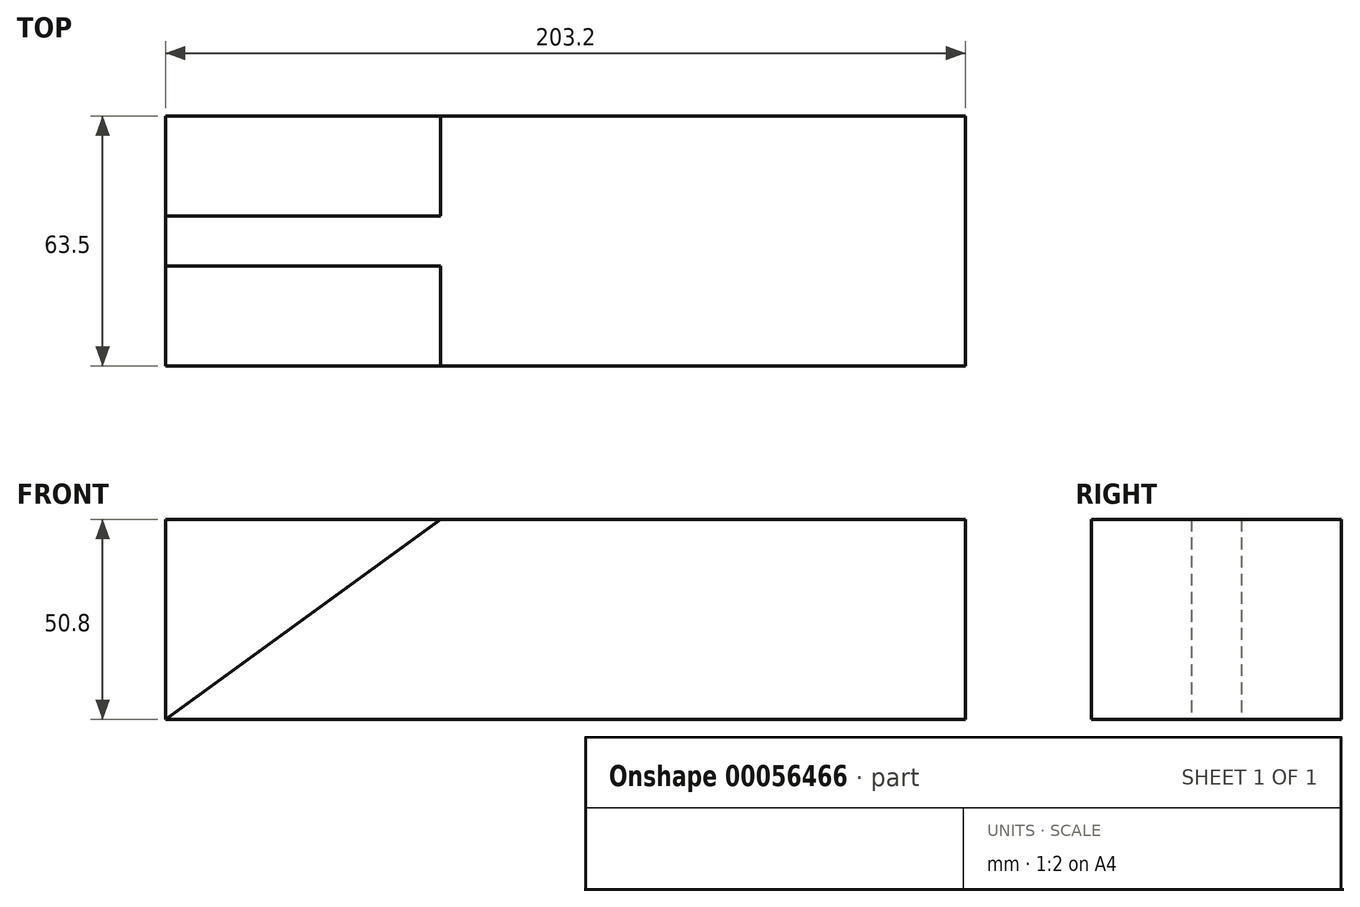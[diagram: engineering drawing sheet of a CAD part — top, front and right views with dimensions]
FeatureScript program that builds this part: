
annotation { "Feature Type Name" : "Feature", "Feature Type Description" : "" }
export const myFeature = defineFeature(function(context is Context, id is Id, definition is map)
    precondition{}
    {
        {
            var Q0;
            Q0=qCreatedBy(makeId("Front.planeOp"),FACE);
            var sketch = newSketch(context, id + "F0", { "sketchPlane" : qUnion([Q0])});
            skLineSegment(sketch, "E0.bottom", {"start": v(-124.46, 40.25) * mm, "end": v(78.74, 40.25) * mm});
            skLineSegment(sketch, "E0.top", {"start": v(-124.46, -10.55) * mm, "end": v(78.74, -10.55) * mm});
            skLineSegment(sketch, "E0.left", {"start": v(-124.46, 40.25) * mm, "end": v(-124.46, -10.55) * mm});
            skLineSegment(sketch, "E0.right", {"start": v(78.74, 40.25) * mm, "end": v(78.74, -10.55) * mm});
            skSolve(sketch);
        }
        {
            var Q0;
            Q0=makeQuery(id+"F0.imprint","IMPRINT",FACE,{"disambiguationData":[TD([[makeQuery(id+"F0.imprint","IMPRINT",EDGE,{"derivedFrom":sQuery(id+"F0.wireOp",EDGE,"E0.bottom")}),-1.0]])]});
            extrude(context, id + "F1", {"entities" : qUnion([Q0]), "depth" : 63.5 * mm});
        }
        {
            var Q0;
            Q0=makeQuery(id+"F1.opExtrude","CAP_FACE",FACE,{"disambiguationData":[OSD([sQuery(id+"F0.wireOp",EDGE,"E0.bottom"),sQuery(id+"F0.wireOp",EDGE,"E0.top"),sQuery(id+"F0.wireOp",EDGE,"E0.left"),sQuery(id+"F0.wireOp",EDGE,"E0.right")])],"isStart":false});
            var sketch = newSketch(context, id + "F2", { "sketchPlane" : qUnion([Q0])});
            skLineSegment(sketch, "E1", {"start": v(-124.46, -10.55) * mm, "end": v(-54.6, 40.25) * mm});
            skSolve(sketch);
        }
        {
            var Q0;
            {var subQ0=sQuery(id+"F2.wireOp",EDGE,"E1");Q0=makeQuery(id+"F2.imprint","IMPRINT",FACE,{"disambiguationData":[TD([[makeQuery(id+"F2.imprint","IMPRINT",EDGE,{"derivedFrom":subQ0}),1.0]])]});}
            extrude(context, id + "F3", {"entities" : qUnion([Q0]), "operationType" : NewBodyOperationType.REMOVE, "oppositeDirection" : true, "depth" : 25.4 * mm});
        }
        {
            var Q0;
            Q0=makeQuery(id+"F1.opExtrude","CAP_FACE",FACE,{"disambiguationData":[OSD([sQuery(id+"F0.wireOp",EDGE,"E0.bottom"),sQuery(id+"F0.wireOp",EDGE,"E0.top"),sQuery(id+"F0.wireOp",EDGE,"E0.left"),sQuery(id+"F0.wireOp",EDGE,"E0.right")])],"isStart":true});
            var sketch = newSketch(context, id + "F4", { "sketchPlane" : qUnion([Q0])});
            skLineSegment(sketch, "E2", {"start": v(124.46, -10.55) * mm, "end": v(54.6, 40.25) * mm});
            skSolve(sketch);
        }
        {
            var Q0;
            {var subQ0=sQuery(id+"F4.wireOp",EDGE,"E2");Q0=makeQuery(id+"F4.imprint","IMPRINT",FACE,{"disambiguationData":[TD([[makeQuery(id+"F4.imprint","IMPRINT",EDGE,{"derivedFrom":subQ0}),-1.0]])]});}
            extrude(context, id + "F5", {"entities" : qUnion([Q0]), "operationType" : NewBodyOperationType.REMOVE, "oppositeDirection" : true, "depth" : 25.4 * mm});
        }
    });
